# Revit family: Erdungs-System_Fang-Erdeinführungsstange_beidseitig_angekuppt
name_source: partatom
category: Generic Models
revit_build: Autodesk Revit 2015 (Build: 20140606_1530(x64)
units: mm (PartAtom-declared; Revit-internal decimal feet)

## types (4) — shared parameters
Manufacturer = OBO Bettermann
Outer Diameter Dimension = 16 mm  [stored 0.0524934 ft]
URL = http://www.obo-bettermann.com

## per-type parameters (varying)
| type | GTIN | Manufacturer Art. No. | Material |
| 101 A-1500 | 4012195427575 | 5400155 | Steel, Galvanized |
| 200 V4A-1500 | 4012195751571 | 5420504 | Stainless Steel AISI 304 |
| 200 V4A-2000 | 4012195331575 | 5420539 | Stainless Steel AISI 304 |
| 101 A-CU | 4012195629054 | 5400627 | Copper |

note: column(s) folded — value = type name in every type: Article Type

note: [stored X ft] marks values corroborated as IEEE doubles in the binary element streams (Revit-internal decimal feet)

## geometry (parser evidence)
native form markers: Sweep x2
no freeform markers — native parametric forms only
